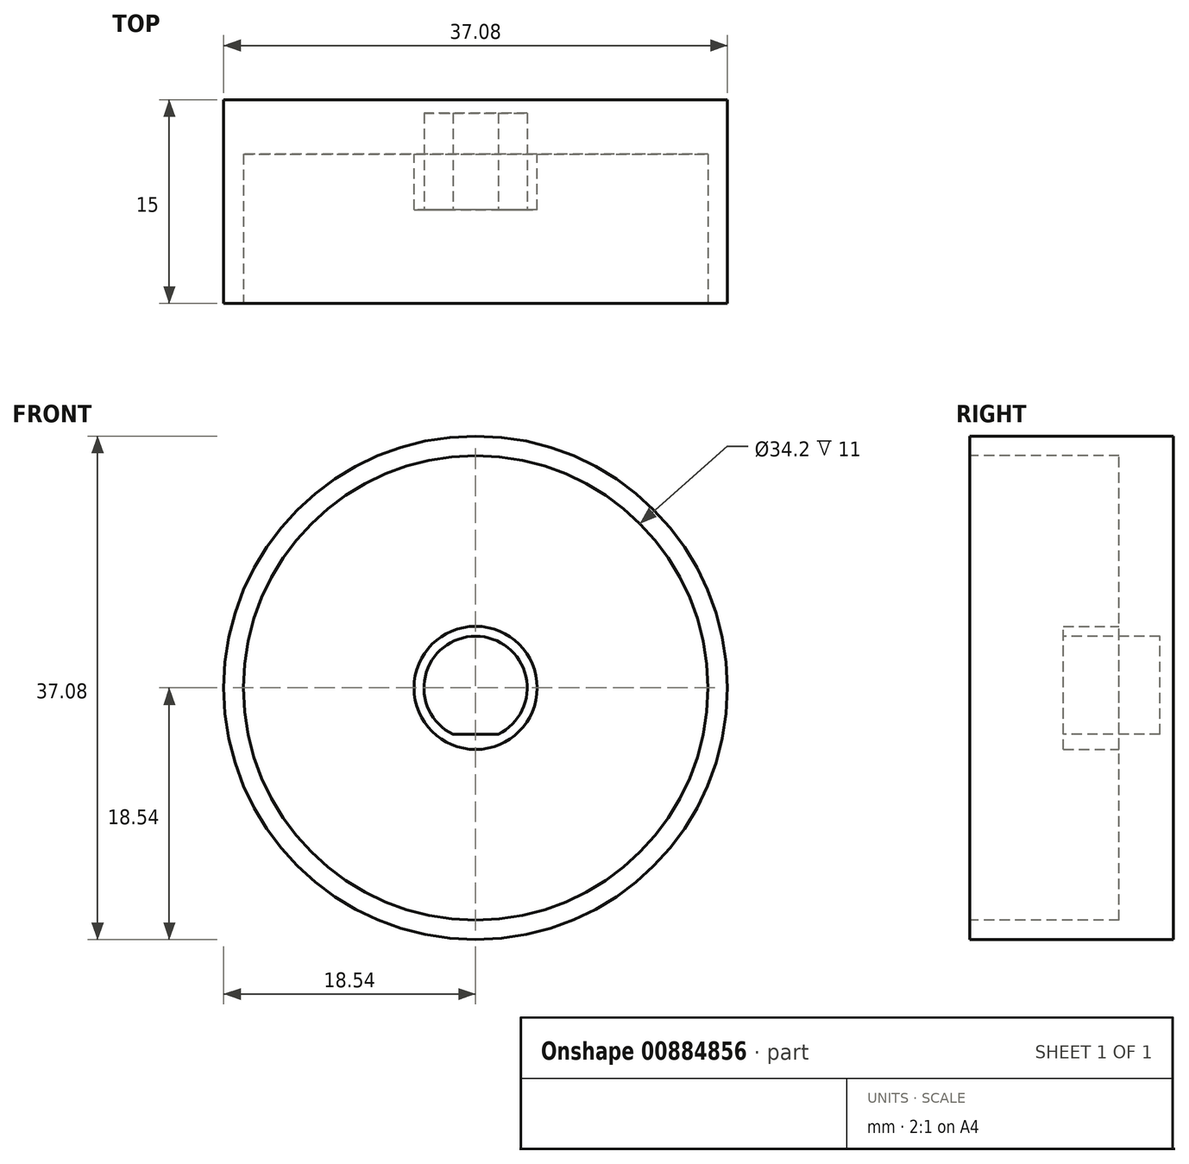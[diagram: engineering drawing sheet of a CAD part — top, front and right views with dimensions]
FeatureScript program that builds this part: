
annotation { "Feature Type Name" : "Feature", "Feature Type Description" : "" }
export const myFeature = defineFeature(function(context is Context, id is Id, definition is map)
    precondition{}
    {
        {
            var Q0;
            Q0=qCreatedBy(makeId("Front.planeOp"),FACE);
            var sketch = newSketch(context, id + "F0", { "sketchPlane" : qUnion([Q0])});
            skCircle(sketch, "E0", {"center": v(0, 0) * mm, "radius": 18.54 * mm});
            skCircle(sketch, "E1", {"center": v(0, 0) * mm, "radius": 4.54 * mm});
            skLineSegment(sketch, "E2", {"start": v(-2.5, -3.78) * mm, "end": v(2.5, -3.78) * mm});
            skSolve(sketch);
        }
        {
            var Q0;
            Q0=makeQuery(id+"F0.imprint","IMPRINT",FACE,{"disambiguationData":[TD([[makeQuery(id+"F0.imprint","IMPRINT",EDGE,{"derivedFrom":sQuery(id+"F0.wireOp",EDGE,"E0")}),1.0]])]});
            var Q1;
            {var subQ0=sQuery(id+"F0.wireOp",EDGE,"E2");Q1=makeQuery(id+"F0.imprint","IMPRINT",FACE,{"disambiguationData":[TD([[makeQuery(id+"F0.imprint","IMPRINT",EDGE,{"derivedFrom":subQ0}),1.0]])]});}
            var Q2;
            {var subQ0=sQuery(id+"F0.wireOp",EDGE,"E2");Q2=makeQuery(id+"F0.imprint","IMPRINT",FACE,{"disambiguationData":[TD([[makeQuery(id+"F0.imprint","IMPRINT",EDGE,{"derivedFrom":subQ0}),-1.0]])]});}
            extrude(context, id + "F1", {"entities" : qUnion([Q0, Q1, Q2]), "depth" : 15 * mm, "offsetDistance" : 25 * mm});
        }
        {
            var Q0;
            Q0=makeQuery(id+"F1.opExtrude","CAP_FACE",FACE,{"disambiguationData":[OSD([sQuery(id+"F0.wireOp",EDGE,"E0")])],"isStart":false});
            var sketch = newSketch(context, id + "F2", { "sketchPlane" : qUnion([Q0])});
            skCircle(sketch, "E3", {"center": v(0, 0) * mm, "radius": 17.1 * mm});
            skSolve(sketch);
        }
        {
            var Q0;
            Q0=makeQuery(id+"F2.imprint","IMPRINT",FACE,{"disambiguationData":[TD([[makeQuery(id+"F2.imprint","IMPRINT",EDGE,{"derivedFrom":sQuery(id+"F2.wireOp",EDGE,"E3")}),1.0]])]});
            extrude(context, id + "F3", {"entities" : qUnion([Q0]), "operationType" : NewBodyOperationType.REMOVE, "oppositeDirection" : true, "depth" : 11 * mm, "offsetDistance" : 25 * mm});
        }
        {
            var Q0;
            Q0=makeQuery(id+"F3.boolean.opBoolean","COPY",FACE,{"derivedFrom":makeQuery(id+"F3.opExtrude","CAP_FACE",FACE,{"disambiguationData":[OSD([sQuery(id+"F2.wireOp",EDGE,"E3")])],"isStart":false})});
            var sketch = newSketch(context, id + "F4", { "sketchPlane" : qUnion([Q0])});
            skSolve(sketch);
        }
        {
            var Q0;
            Q0=makeQuery(id+"F4.imprint","IMPRINT",FACE,{"disambiguationData":[TD([[makeQuery(id+"F4.imprint","IMPRINT",EDGE,{"derivedFrom":makeQuery(id+"F3.boolean.opBoolean","COPY",EDGE,{"derivedFrom":makeQuery(id+"F3.opExtrude","CAP_EDGE",EDGE,{"disambiguationData":[OSD([sQuery(id+"F2.wireOp",EDGE,"E3")])],"isStart":false})})}),1.0]])]});
            var sketch = newSketch(context, id + "F5", { "sketchPlane" : qUnion([Q0])});
            skCircle(sketch, "E4", {"center": v(0, 0) * mm, "radius": 4.54 * mm});
            skSolve(sketch);
        }
        {
            var Q0;
            Q0=makeQuery(id+"F5.imprint","IMPRINT",FACE,{"disambiguationData":[TD([[makeQuery(id+"F5.imprint","IMPRINT",EDGE,{"derivedFrom":sQuery(id+"F5.wireOp",EDGE,"E4")}),1.0]])]});
            extrude(context, id + "F6", {"entities" : qUnion([Q0]), "operationType" : NewBodyOperationType.ADD, "depth" : 6 * mm, "offsetDistance" : 25 * mm});
        }
        {
            var Q0;
            Q0=makeQuery(id+"F6.opExtrude","CAP_FACE",FACE,{"disambiguationData":[OSD([sQuery(id+"F5.wireOp",EDGE,"E4")])],"isStart":false});
            var sketch = newSketch(context, id + "F7", { "sketchPlane" : qUnion([Q0])});
            skSolve(sketch);
        }
        {
            var Q0;
            Q0=makeQuery(id+"F7.imprint","IMPRINT",FACE,{"disambiguationData":[TD([[makeQuery(id+"F7.imprint","IMPRINT",EDGE,{"derivedFrom":makeQuery(id+"F6.opExtrude","CAP_EDGE",EDGE,{"disambiguationData":[OSD([sQuery(id+"F5.wireOp",EDGE,"E4")])],"isStart":false})}),1.0]])]});
            var sketch = newSketch(context, id + "F8", { "sketchPlane" : qUnion([Q0])});
            skCircle(sketch, "E5", {"center": v(0, 0) * mm, "radius": 3.8 * mm});
            skLineSegment(sketch, "E6", {"start": v(-1.66, -3.42) * mm, "end": v(1.66, -3.42) * mm});
            skSolve(sketch);
        }
        {
            var Q0;
            {var subQ0=sQuery(id+"F8.wireOp",EDGE,"E6");Q0=makeQuery(id+"F8.imprint","IMPRINT",FACE,{"disambiguationData":[TD([[makeQuery(id+"F8.imprint","IMPRINT",EDGE,{"derivedFrom":subQ0}),1.0]])]});}
            extrude(context, id + "F9", {"entities" : qUnion([Q0]), "operationType" : NewBodyOperationType.REMOVE, "oppositeDirection" : true, "depth" : 9 * mm, "offsetDistance" : 25 * mm});
        }
        {
            var Q0;
            Q0=makeQuery(id+"F7.imprint","IMPRINT",FACE,{"disambiguationData":[TD([[makeQuery(id+"F7.imprint","IMPRINT",EDGE,{"derivedFrom":makeQuery(id+"F6.opExtrude","CAP_EDGE",EDGE,{"disambiguationData":[OSD([sQuery(id+"F5.wireOp",EDGE,"E4")])],"isStart":false})}),1.0]])]});
            extrude(context, id + "F10", {"entities" : qUnion([Q0]), "operationType" : NewBodyOperationType.ADD, "depth" : 1.5 * mm, "offsetDistance" : 25 * mm});
        }
        {
            var Q0;
            Q0=makeQuery(id+"F10.opExtrude","CAP_FACE",FACE,{"disambiguationData":[OSD([sQuery(id+"F5.wireOp",EDGE,"E4")])],"isStart":false});
            extrude(context, id + "F11", {"entities" : qUnion([Q0]), "operationType" : NewBodyOperationType.REMOVE, "oppositeDirection" : true, "depth" : 3.4 * mm, "offsetDistance" : 25 * mm});
        }
    });
